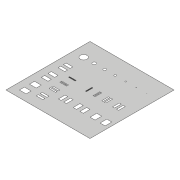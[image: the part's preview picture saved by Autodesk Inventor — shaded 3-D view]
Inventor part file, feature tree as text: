
AUTODESK INVENTOR PART (.ipt)
format: ipt  version: 2019 (Build 230136000, 136)  size: 483,328 bytes
history: native  units: mm
features: extrude x9, sketch x9
ambient origin geometry x8: Origin, YZ Plane, XZ Plane, XY Plane, X Axis, Y Axis, Z Axis, Center Point
bodies: Solid1 (feature_tree)
feature tree (18):
  extrude  "Extrusion1"  Depth=0.125mm
  extrude  "Extrusion3"  Depth=0.125mm
  extrude  "Extrusion2"  Depth=0.02mm
  extrude  "Extrusion4"  Depth=0.008mm
  sketch  "Sketch6"  dims[d9=0.006mm d10=0.004mm]
  extrude  "Extrusion5"  Depth=0.004mm
  extrude  "Extrusion6"  Depth=0.15mm
  sketch  "Sketch8"  dims[d13=0.02625mm d14=0.02625mm]
  extrude  "Extrusion7"  Depth=0.02625mm
  extrude  "Extrusion8"  Depth=0.02625mm
  extrude  "Extrusion9"  Depth=10.0mm
  sketch  "Sketch1"  dims[d0=0.25mm d1=0.125mm]
  sketch  "Sketch2"  dims[d2=0.25mm d3=0.125mm]
  sketch  "Sketch3"  dims[d4=5e-05mm d5=0.0mm d6=0.02mm]
  sketch  "Sketch5"  dims[d7=0.01mm d8=0.008mm]
  sketch  "Sketch7"  dims[d11=0.002mm d12=0.15mm]
  sketch  "Sketch9"  dims[d15=0.02625mm d16=0.02625mm]
  sketch  "Sketch10"  dims[d17=0.02625mm d18=0.02625mm d19=0.001mm d20=0.02625mm d21=0.0002mm d22=0.0mm d24=0.0mm d25=0.03mm d26=0.01mm d27=0.02mm d30=0.01mm d31=0.02mm d34=0.01mm d35=0.008mm d36=0.02mm d37=0.008mm d38=0.02mm d39=0.008mm d40=0.02mm d41=0.006mm d42=0.02mm d43=0.006mm d44=0.02mm d45=0.006mm d46=0.004mm d47=0.02mm d48=0.004mm d49=0.02mm d50=0.004mm d51=0.002mm d52=0.02mm d53=0.002mm d54=0.02mm d55=0.002mm d56=0.02mm d57=0.02mm d58=0.02mm d59=0.001mm d60=0.02mm d61=0.001mm d62=0.02mm d63=0.001mm d64=0.02mm d65=10.0mm d66=0.0mm d68=0.018mm d108=0.03mm d109=0.02mm d110=0.01mm d111=0.01mm d112=0.02mm d113=0.01mm d114=0.02mm d115=0.008mm d116=0.008mm d117=0.02mm d118=0.008mm d119=0.02mm d120=0.006mm d121=0.006mm d122=0.02mm d123=0.006mm d124=0.02mm d125=0.004mm d126=0.004mm d127=0.02mm d128=0.004mm d129=0.02mm d130=0.02mm d131=0.02mm d132=0.02mm d133=0.002mm d134=0.002mm d135=0.02mm d136=0.002mm d137=0.02mm d138=0.001mm d139=0.001mm d140=0.02mm d141=0.001mm d142=0.0mm d143=0.02mm d144=0.02mm d145=0.02mm d146=10.0mm d147=0.0mm d148=0.0mm d149=0.0mm d150=0.0mm d151=0.0mm d152=0.0mm d153=0.0mm d154=0.0mm d155=0.0mm d156=0.0mm d158=0.015mm d159=0.02mm d160=0.015mm d161=0.02mm d162=0.015mm d163=0.02mm d164=0.01mm d166=0.006mm d167=0.02mm d168=0.006mm d169=0.02mm d170=0.006mm d171=0.004mm d172=0.02mm d173=0.004mm d174=0.02mm d175=0.004mm d176=0.002mm d177=0.02mm d178=0.002mm d179=0.02mm d180=0.002mm d181=0.02mm d182=0.02mm d183=0.001mm d184=0.02mm d185=0.001mm d186=0.02mm d187=0.001mm d188=0.02mm d190=0.02mm d191=0.02mm d192=0.02mm d194=0.03mm d195=0.0mm d196=0.01mm d197=0.02mm d198=0.01mm d199=0.02mm d200=0.01mm d201=0.008mm d202=0.02mm d203=0.008mm d204=0.02mm d205=0.008mm d206=0.02mm d207=0.015mm d208=0.02mm d209=0.015mm d210=0.02mm d211=0.015mm d212=0.02mm d213=0.07mm d214=10.0mm d215=0.0mm d216=10.0mm d217=0.0mm d218=0.02mm d219=0.02mm d220=0.006mm d221=0.006mm d222=0.02mm d223=0.006mm d224=0.02mm d225=0.004mm d226=0.004mm d227=0.02mm d228=0.004mm d229=0.02mm d230=0.02mm d231=0.002mm d232=0.002mm d233=0.02mm d234=0.002mm d235=0.02mm d236=0.001mm d237=0.001mm d238=0.02mm d239=0.001mm d240=0.0mm d241=0.02mm d242=0.02mm d243=0.0mm d244=0.0mm d245=0.0mm d246=0.0mm d247=0.0mm d248=0.0mm d249=0.0mm d250=0.02mm d251=0.02mm d252=0.125mm d253=0.03mm d255=0.02mm d256=0.01mm d257=0.01mm d258=0.02mm d259=0.01mm d260=0.02mm d261=0.008mm d262=0.008mm d263=0.02mm d264=0.008mm d265=0.02mm d267=0.0mm d268=0.0mm d269=0.065mm d270=0.02mm d271=0.015mm d272=0.015mm d273=0.02mm d274=0.015mm d275=0.02mm d276=0.01mm d277=10.0mm d278=0.0mm d279=10.0mm d280=0.0mm d281=0.02mm d282=0.01mm d283=0.008mm d284=0.006mm d285=0.004mm d286=0.002mm d294=0.001mm d297=0.05mm d298=0.03125mm d299=0.03125mm d300=0.03125mm d301=0.03125mm d302=0.03125mm d303=0.03125mm d304=0.03125mm d305=10.0mm d306=0.0mm]
